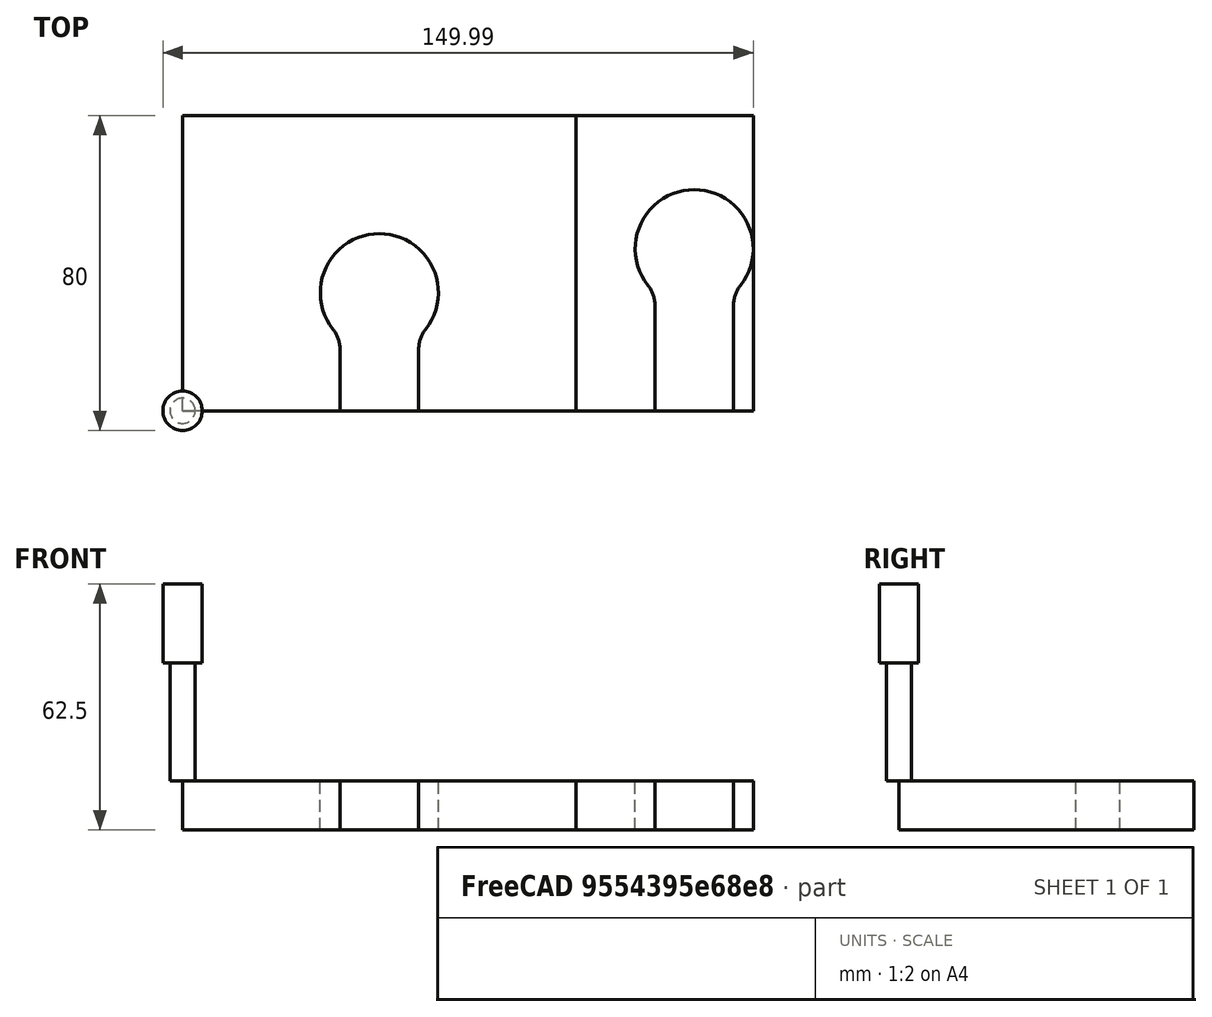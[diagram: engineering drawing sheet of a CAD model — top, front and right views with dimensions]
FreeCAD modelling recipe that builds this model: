
FCSTD DOCUMENT  (FreeCAD 0.19R14555 (Git shallow))
Label: Keyhole2
License: All rights reserved
LicenseURL: http://en.wikipedia.org/wiki/All_rights_reserved
objects: Part::FeaturePython×5, Path::FeaturePython×4, Sketcher::SketchObject×2, PartDesign::Pad×2, Mesh::FeaturePython×2, PartDesign::Fillet×2, PartDesign::Body×2, App::Part×2, App::DocumentObjectGroup×2, App::FeaturePython×1, Path::FeatureCompoundPython×1
note: 19 computed .brp shape members not serialized (recipe doc carries the construction recipe); baked Part::Feature solids carry a one-line shape summary decoded from their .brp

FEATURE [Sketcher::SketchObject] Sketch
  FullyConstrained = true
  MapMode = 5
  Support = -> [XY_Plane001]
  sketch-geometry (8):
    g0: LineSegment StartX=0 StartY=75 StartZ=0 EndX=100 EndY=75 EndZ=0
    g1: LineSegment StartX=100 StartY=75 StartZ=0 EndX=100 EndY=0 EndZ=0
    g2: LineSegment StartX=100 StartY=0 StartZ=0 EndX=60 EndY=0 EndZ=0
    g3: LineSegment StartX=0 StartY=0 StartZ=0 EndX=0 EndY=75 EndZ=0
    g4: ArcOfCircle CenterX=50 CenterY=30 CenterZ=0 NormalX=0 NormalY=0 NormalZ=1 AngleXU=0 Radius=15 StartAngle=5.44212 EndAngle=10.2658
    g5: LineSegment StartX=40 StartY=0 StartZ=0 EndX=40 EndY=18.8197 EndZ=0
    g6: LineSegment StartX=60 StartY=0 StartZ=0 EndX=60 EndY=18.8197 EndZ=0
    g7: LineSegment StartX=40 StartY=0 StartZ=0 EndX=0 EndY=0 EndZ=0
  constraints (23):
    c: Coincident(g0,g1)
    c: Coincident(g1,g2)
    c: Coincident(g7,g3)
    c: Coincident(g3,g0)
    c: Horizontal(g0)
    c: Horizontal(g2)
    c: Vertical(g1)
    c: Vertical(g3)
    c: Coincident(g7,g-1)
    c: DistanceX(g7,g2) = 100
    c: DistanceY(g3,g3) = 75
    c: Diameter(g4) = 30
    c: DistanceX(g7,g4) = 50
    c: DistanceY(g7,g4) = 30
    c: Perpendicular(g2,g5)
    c: Perpendicular(g2,g6)
    c: DistanceX(g7,g5) = 40
    c: DistanceX(g7,g6) = 60
    c: Coincident(g4,g6)
    c: Coincident(g4,g5)
    c: Coincident(g2,g6)
    c: Coincident(g7,g5)
    c: Tangent(g2,g7)
FEATURE [PartDesign::Pad] Pad
  Direction = (1,1,1)
  Length = 12.5
  Length2 = 100
  Profile = -> Sketch
  Refine = true
  Reversed = true
  Type = 0
FEATURE [Mesh::FeaturePython] CutMaterial  # WARN: FeaturePython — macro-defined, semantics opaque (R4)
FEATURE [PartDesign::Fillet] Fillet
  Base = -> Pad [Edge20,Edge17]
  BaseFeature = -> Pad
  Radius = 8
  SupportTransform = false
FEATURE [PartDesign::Body] Body
  Group = -> [Sketch,Pad,Fillet]
  Origin = -> Origin001
  Tip = -> Fillet
FEATURE [App::Part] Part  label="Female"
  Group = -> [Body]
  Origin = -> Origin
FEATURE [Sketcher::SketchObject] Sketch001
  FullyConstrained = true
  MapMode = 5
  Support = -> [XY_Plane003]
  sketch-geometry (4):
    g0: LineSegment StartX=139.99 StartY=30 StartZ=0 EndX=139.99 EndY=0 EndZ=0
    g1: LineSegment StartX=139.99 StartY=0 StartZ=0 EndX=120 EndY=0 EndZ=0
    g2: LineSegment StartX=120 StartY=0 StartZ=0 EndX=120 EndY=30 EndZ=0
    g3: ArcOfCircle CenterX=129.995 CenterY=41.1781 CenterZ=0 NormalX=0 NormalY=0 NormalZ=1 AngleXU=0 Radius=14.995 StartAngle=5.44197 EndAngle=10.266
  constraints (13):
    c: Horizontal(g1)
    c: Vertical(g0)
    c: Vertical(g2)
    c: DistanceY(g0,g0) = 30
    c: DistanceX(g1,g1) = 19.99
    c: Diameter(g3) = 29.99
    c: Coincident(g2,g3)
    c: Coincident(g0,g3)
    c: Coincident(g2,g1)
    c: Coincident(g0,g1)
    c: DistanceY(g2,g2) = 30
    c: DistanceX(g1,g-1) = -120
    c: DistanceY(g-1,g1) = 0
FEATURE [PartDesign::Pad] Pad001
  Direction = (1,1,1)
  Length = 12.5
  Length2 = 100
  Profile = -> Sketch001
  Reversed = true
  Type = 0
FEATURE [PartDesign::Fillet] Fillet001
  Base = -> Pad001 [Edge8,Edge1]
  BaseFeature = -> Pad001
  Radius = 8
  SupportTransform = false
FEATURE [PartDesign::Body] Body001
  Group = -> [Sketch001,Pad001,Fillet001]
  Origin = -> Origin003
  Tip = -> Fillet001
FEATURE [App::Part] Part001  label="Male"
  Group = -> [Body001]
  Origin = -> Origin002
FEATURE [Part::FeaturePython] ToolBit002  label="6.4mm Endmill"  # Path/CAM toolbit (typed FeaturePython)
  BitPropertyNames = Chipload | CuttingEdgeHeight | Diameter | Flutes | Length | Material | ShankDiameter
  BitShape = /app/freecad/Mod/Path/Tools/Shape/endmill.fcstd
  Chipload = 0
  CuttingEdgeHeight = 30
  Diameter = 6.4
  File = <userpath>/Documents/MensShed/FreeCAD/Bit/6.4mm_Endmill.fctb
  Flutes = 0
  Length = 50
  Material = 0
  ShankDiameter = 10
  ShapeName = endmill
FEATURE [Path::FeaturePython] Profile001  # Path/CAM operation (typed FeaturePython)
  Active = true
  AttemptInverseAngle = false
  ClearanceHeight = 0
  Direction = 0
  EnableRotation = 0
  FinalDepth = 0
  HandleMultipleFeatures = 0
  InverseAngle = false
  JoinType = 0
  LimitDepthToFace = false
  MiterLimit = 0
  OffsetExtra = 0
  OpFinalDepth = 0
  OpStartDepth = 0
  OpStockZMax = 0
  OpStockZMin = 0
  OpToolDiameter = 0
  ReverseDirection = false
  SafeHeight = 0
  Side = 0
  StartDepth = 0
  StartPoint = (0,0,0)
  StepDown = 0
  UseComp = false
  UseStartPoint = false
  processCircles = false
  processHoles = false
  processPerimeter = false
FEATURE [App::FeaturePython] SetupSheet  # Path/CAM operation (typed FeaturePython)
  ClearanceHeightExpression = OpStockZMax+SetupSheet.ClearanceHeightOffset
  ClearanceHeightOffset = 5
  CoolantMode = 0
  CoolantModes = None | Flood | Mist
  FinalDepthExpression = OpFinalDepth
  HorizRapid = 0
  SafeHeightExpression = OpStockZMax+SetupSheet.SafeHeightOffset
  SafeHeightOffset = 3
  StartDepthExpression = OpStartDepth
  StepDownExpression = OpToolDiameter
  VertRapid = 0
FEATURE [Part::FeaturePython] Clone  label="Model-Female"  # Draft clone (typed FeaturePython)
  AttacherType = Attacher::AttachEngine3D
  Fuse = false
  Objects = -> [Part]
  PathResource = Model
  Scale = (1,1,1)
FEATURE [Part::FeaturePython] Clone001  label="Model-Male"  # Draft clone (typed FeaturePython)
  AttacherType = Attacher::AttachEngine3D
  Fuse = false
  Objects = -> [Part001]
  PathResource = Model
  Scale = (1,1,1)
FEATURE [App::DocumentObjectGroup] Model
  Group = -> [Clone,Clone001]
FEATURE [Part::FeaturePython] Stock001  # WARN: FeaturePython — macro-defined, semantics opaque (R4)
  Height = 12.5
  Length = 144.99
  Placement = pos=(0,0,-12.5) rot=(0,0,1;0rad)
  StockType = CreateBox
  Width = 75
FEATURE [Part::FeaturePython] ToolBit003  label="6.4mm Endmill001"  # Path/CAM toolbit (typed FeaturePython)
  BitPropertyNames = Chipload | CuttingEdgeHeight | Diameter | Flutes | Length | Material | ShankDiameter
  BitShape = /app/freecad/Mod/Path/Tools/Shape/endmill.fcstd
  Chipload = 0
  CuttingEdgeHeight = 30
  Diameter = 6.4
  File = <userpath>/Documents/MensShed/FreeCAD/Bit/6.4mm_Endmill.fctb
  Flutes = 0
  Length = 50
  Material = 0
  ShankDiameter = 10
  ShapeName = endmill
FEATURE [Path::FeaturePython] __4mm_Endmill001  label="6.4mm Endmill002"  # Path/CAM operation (typed FeaturePython)
  HorizFeed = 40
  HorizRapid = 0
  SpindleDir = 0
  SpindleSpeed = 10000
  Tool = -> ToolBit003
  ToolNumber = 1
  VertFeed = 40
  VertRapid = 0
  expr: HorizRapid = SetupSheet.HorizRapid
  expr: VertRapid = SetupSheet.VertRapid
FEATURE [App::DocumentObjectGroup] Tools
  Group = -> [__4mm_Endmill001]
FEATURE [Path::FeaturePython] Profile  # Path/CAM operation (typed FeaturePython)
  Active = true
  AreaParams:
    Tolerance = 1e-07
    FitArcs = True
    Simplify = False
    CleanDistance = 0.0
    Accuracy = 0.01
    Unit = 1.0
    MinArcPoints = 4
    MaxArcPoints = 100
    ClipperScale = 10000000.0
    Fill = 0
    Coplanar = 0
    Reorient = True
    Outline = False
    Explode = False
    OpenMode = 0
    Deflection = 0.01
    SubjectFill = 0
    ClipFill = 0
    Offset = 3.2
    ExtraPass = 0
    Stepover = 0.0
    LastStepover = 0.0
    JoinType = 0
    EndType = 0
    MiterLimit = 2.0
    RoundPrecision = 0.0
    PocketMode = 0
    ToolRadius = 1.0
    PocketExtraOffset = 0.0
    PocketStepover = 0.0
    PocketLastStepover = 0.0
    FromCenter = False
    Angle = 45.0
    AngleShift = 0.0
    Shift = 0.0
    Thicken = False
    SectionCount = -1
    Stepdown = 1.0
    SectionOffset = 0.0
    SectionTolerance = 1e-06
    SectionMode = 2
    Project = False
  AttemptInverseAngle = true
  Base = -> [Clone,Clone001]
  ClearanceHeight = 5
  CoolantMode = None
  CycleTime = 00:01:15
  Direction = 0
  EnableRotation = 0
  FinalDepth = -12.5
  HandleMultipleFeatures = 0
  InverseAngle = false
  JoinType = 0
  LimitDepthToFace = true
  MiterLimit = 0.1
  OffsetExtra = 0
  OpFinalDepth = 0
  OpStartDepth = 3
  OpStockZMax = 0
  OpStockZMin = -12.5
  OpToolDiameter = 6.4
  PathParams = {'orientation': 1, 'feedrate': 40.0, 'feedrate_v': 40.0, 'verbose': True, 'resume_height': 3.0, 'retraction': 5.0, 'return_end': True, 'preamble': False, 'start': Vector (102.26274165, 77.26274170000012, 5.0)}
  ReverseDirection = false
  SafeHeight = 3
  Side = 0
  StartDepth = 0
  StartPoint = (0,0,0)
  StepDown = 3
  ToolController = -> __4mm_Endmill001
  UseComp = true
  UseStartPoint = false
  processCircles = false
  processHoles = false
  processPerimeter = true
  expr: ClearanceHeight = OpStockZMax + SetupSheet.ClearanceHeightOffset
  expr: SafeHeight = OpStockZMax + SetupSheet.SafeHeightOffset
  expr: StepDown = 3
  expr: FinalDepth = -12.5
  expr: StartDepth = 0
FEATURE [Path::FeatureCompoundPython] Operations  # Path/CAM operation (typed FeaturePython)
  Group = -> [Profile]
  UsePlacements = false
FEATURE [Path::FeaturePython] Job  # Path/CAM operation (typed FeaturePython)
  CycleTime = 00:01:15
  Fixtures = G54
  GeometryTolerance = 0.01
  LastPostProcessDate = 2021-12-08 10:29:11.848044
  LastPostProcessOutput = <userpath>/Documents/MensShed/Keyhole2.ngc
  Model = -> Model
  Operations = -> Operations
  OrderOutputBy = 0
  PostProcessor = 7
  PostProcessorOutputFile = <userpath>/Documents/MensShed/Keyhole2.ngc
  SetupSheet = -> SetupSheet
  SplitOutput = false
  Stock = -> Stock001
  Tools = -> Tools
FEATURE [Mesh::FeaturePython] CutMaterial001  # WARN: FeaturePython — macro-defined, semantics opaque (R4)
